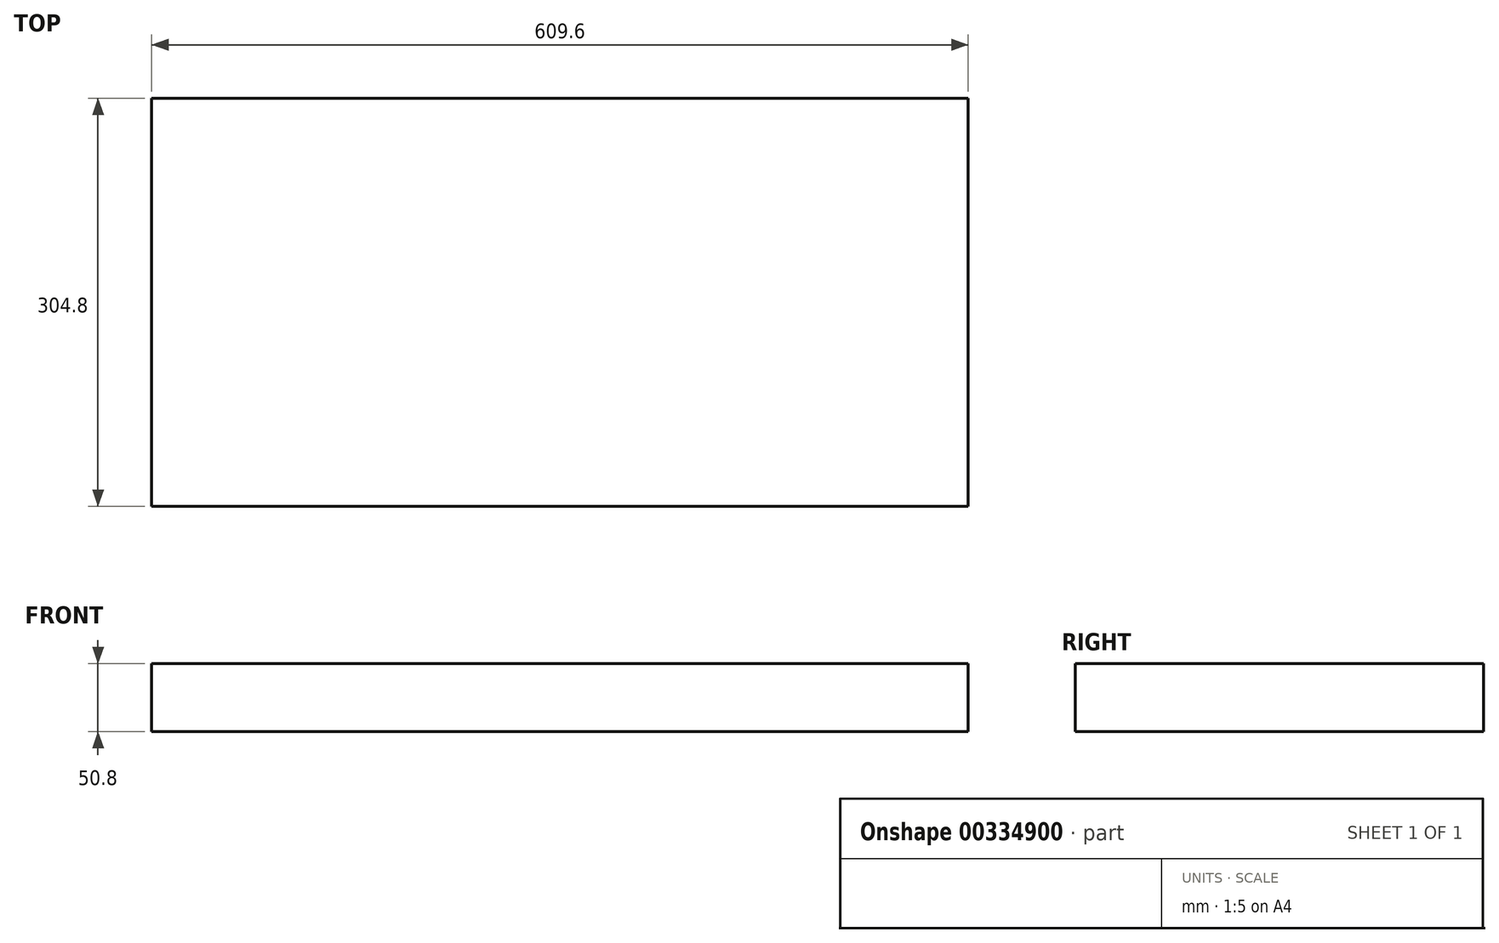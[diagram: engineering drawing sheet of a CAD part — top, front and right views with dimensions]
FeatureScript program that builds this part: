
annotation { "Feature Type Name" : "Feature", "Feature Type Description" : "" }
export const myFeature = defineFeature(function(context is Context, id is Id, definition is map)
    precondition{}
    {
        {
            var Q0;
            Q0=qCreatedBy(makeId("Top.planeOp"),FACE);
            var sketch = newSketch(context, id + "F0", { "sketchPlane" : qUnion([Q0])});
            skLineSegment(sketch, "E0", {"start": v(0, 478.23) * mm, "end": v(609.6, 478.23) * mm});
            skLineSegment(sketch, "E1", {"start": v(609.6, 478.23) * mm, "end": v(609.6, 173.43) * mm});
            skLineSegment(sketch, "E2", {"start": v(609.6, 173.43) * mm, "end": v(0, 173.43) * mm});
            skLineSegment(sketch, "E3", {"start": v(0, 173.43) * mm, "end": v(0, 478.23) * mm});
            skSolve(sketch);
        }
        {
            var Q0;
            Q0 = qSketchRegion(id + "F0", true);
            extrude(context, id + "F1", {"entities" : qUnion([Q0]), "depth" : 50.8 * mm});
        }
    });
